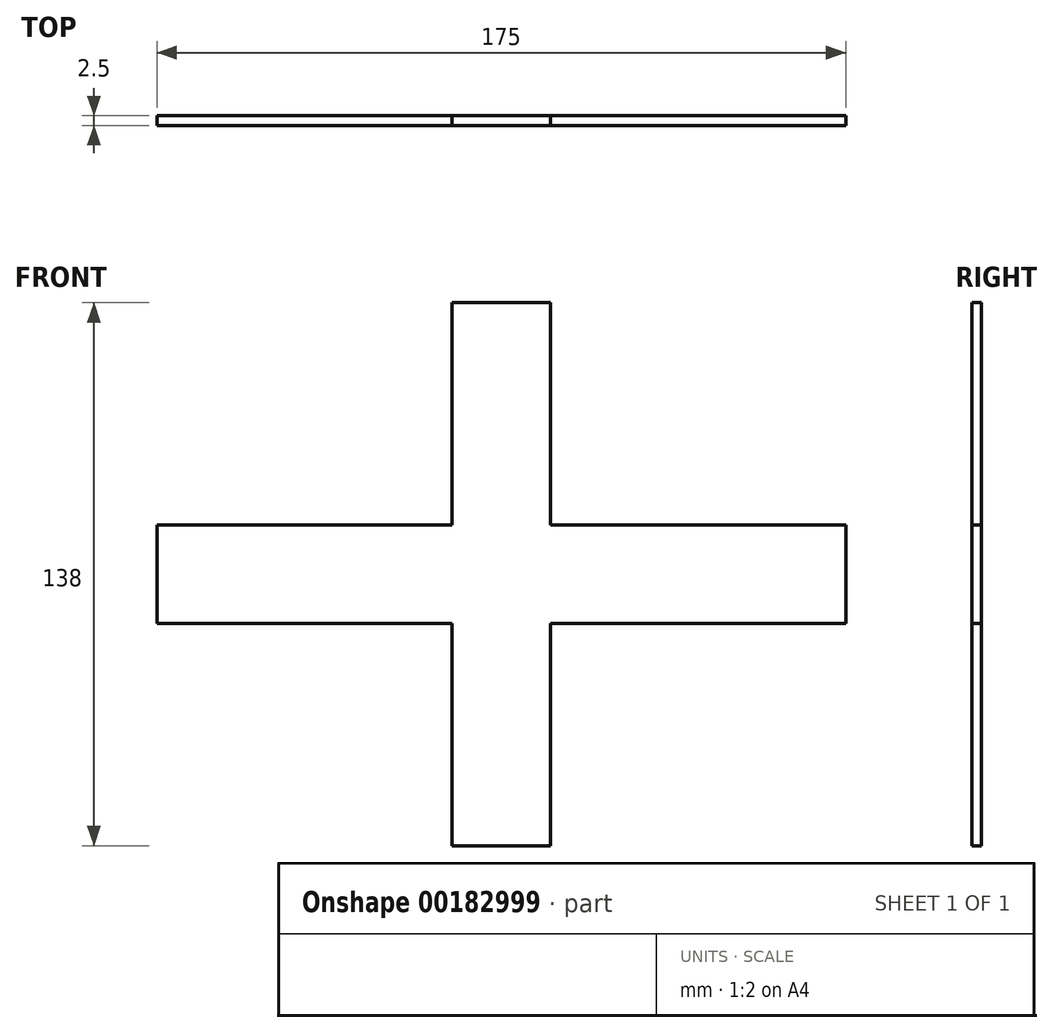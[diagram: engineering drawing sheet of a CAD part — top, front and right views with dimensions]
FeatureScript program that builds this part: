
annotation { "Feature Type Name" : "Feature", "Feature Type Description" : "" }
export const myFeature = defineFeature(function(context is Context, id is Id, definition is map)
    precondition{}
    {
        {
            var Q0;
            Q0=qCreatedBy(makeId("Front.planeOp"),FACE);
            var sketch = newSketch(context, id + "F0", { "sketchPlane" : qUnion([Q0])});
            skLineSegment(sketch, "E0.bottom", {"start": v(87.5, -12.5) * mm, "end": v(-87.5, -12.5) * mm});
            skLineSegment(sketch, "E0.top", {"start": v(87.5, 12.5) * mm, "end": v(-87.5, 12.5) * mm});
            skLineSegment(sketch, "E0.left", {"start": v(87.5, -12.5) * mm, "end": v(87.5, 12.5) * mm});
            skLineSegment(sketch, "E0.right", {"start": v(-87.5, -12.5) * mm, "end": v(-87.5, 12.5) * mm});
            skPoint(sketch, "E0.middle", {"position": v(0, 0) * mm});
            skLineSegment(sketch, "E1.bottom", {"start": v(12.5, -69) * mm, "end": v(-12.5, -69) * mm});
            skLineSegment(sketch, "E1.top", {"start": v(12.5, 69) * mm, "end": v(-12.5, 69) * mm});
            skLineSegment(sketch, "E1.left", {"start": v(12.5, -69) * mm, "end": v(12.5, 69) * mm});
            skLineSegment(sketch, "E1.right", {"start": v(-12.5, -69) * mm, "end": v(-12.5, 69) * mm});
            skSolve(sketch);
        }
        {
            var Q0;
            Q0 = qSketchRegion(id + "F0", true);
            extrude(context, id + "F1", {"entities" : qUnion([Q0]), "depth" : 2.5 * mm});
        }
    });
